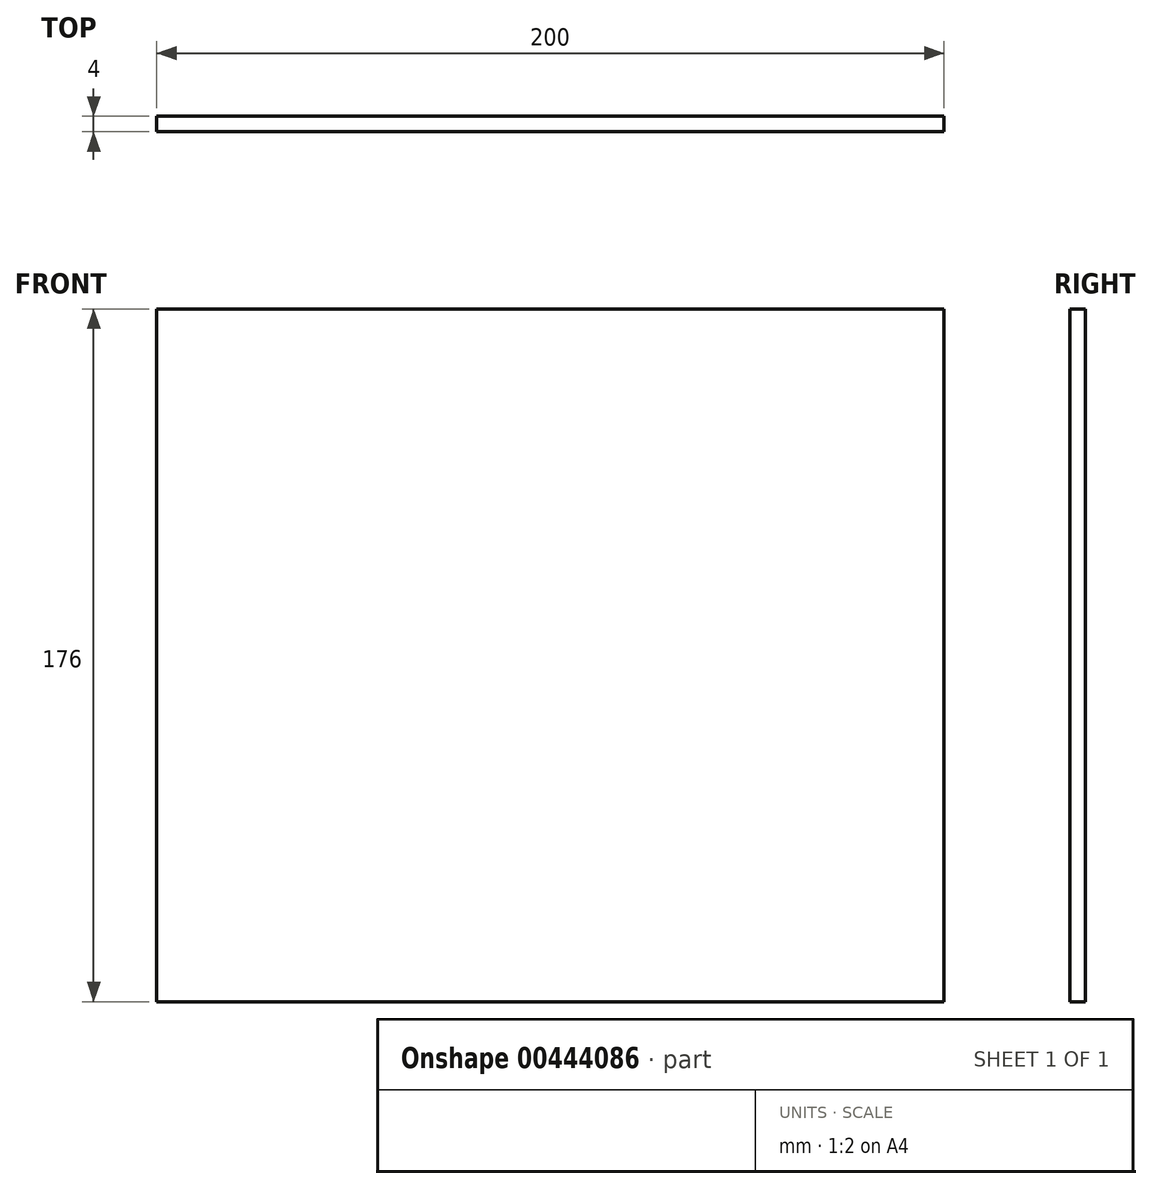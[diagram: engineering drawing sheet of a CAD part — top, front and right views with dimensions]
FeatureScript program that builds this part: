
annotation { "Feature Type Name" : "Feature", "Feature Type Description" : "" }
export const myFeature = defineFeature(function(context is Context, id is Id, definition is map)
    precondition{}
    {
        {
            var Q0;
            Q0=qCreatedBy(makeId("Front.planeOp"),FACE);
            var sketch = newSketch(context, id + "F0", { "sketchPlane" : qUnion([Q0])});
            skLineSegment(sketch, "E0.bottom", {"start": v(-137.52, 140.4) * mm, "end": v(62.48, 140.4) * mm});
            skLineSegment(sketch, "E0.top", {"start": v(-137.52, -35.6) * mm, "end": v(62.48, -35.6) * mm});
            skLineSegment(sketch, "E0.left", {"start": v(-137.52, 140.4) * mm, "end": v(-137.52, -35.6) * mm});
            skLineSegment(sketch, "E0.right", {"start": v(62.48, 140.4) * mm, "end": v(62.48, -35.6) * mm});
            skSolve(sketch);
        }
        {
            var Q0;
            Q0 = qSketchRegion(id + "F0", true);
            extrude(context, id + "F1", {"entities" : qUnion([Q0]), "depth" : 4 * mm});
        }
    });
